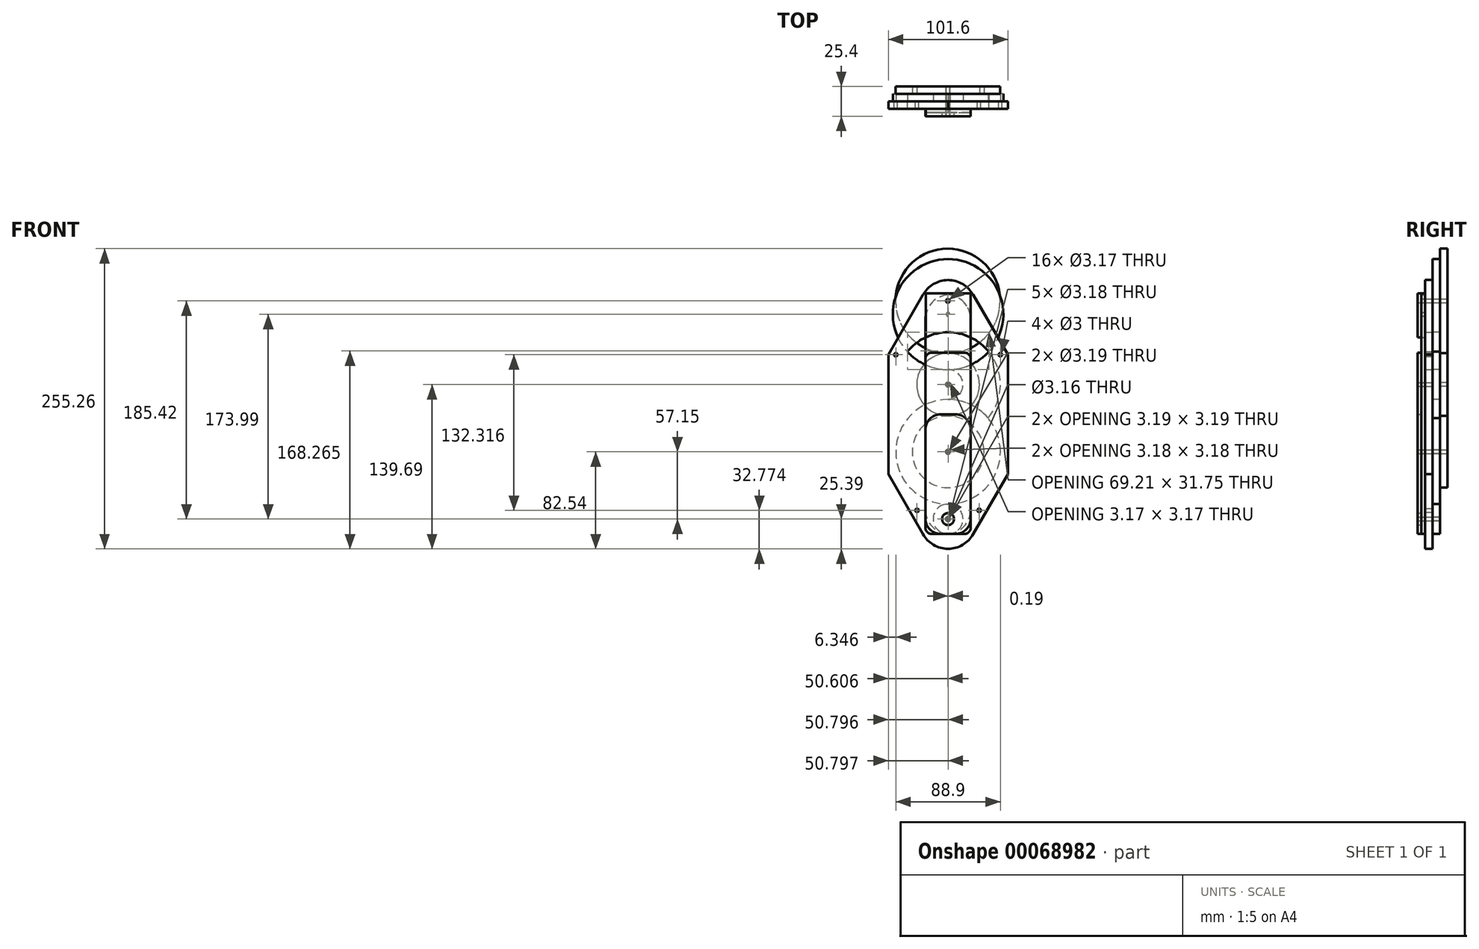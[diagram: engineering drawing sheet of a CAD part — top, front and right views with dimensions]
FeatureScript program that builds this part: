
annotation { "Feature Type Name" : "Feature", "Feature Type Description" : "" }
export const myFeature = defineFeature(function(context is Context, id is Id, definition is map)
    precondition{}
    {
        {
            var Q0;
            Q0=qCreatedBy(makeId("Front.planeOp"),FACE);
            var sketch = newSketch(context, id + "F0", { "sketchPlane" : qUnion([Q0])});
            skLineSegment(sketch, "E0.MirrorCS", {"start": v(51.33, 38.1) * mm, "end": v(22, -12.7) * mm});
            skArc(sketch, "E1.MirrorC", {"start": v(22, -12.7) * mm, "mid": v(12.93, -21.86) * mm, "end": v(0.53, -25.4) * mm});
            skLineSegment(sketch, "E2.MirrorCS", {"start": v(51.33, 38.1) * mm, "end": v(51.33, 88.9) * mm});
            skLineSegment(sketch, "E3", {"start": v(0.53, 88.9) * mm, "end": v(51.33, 88.9) * mm, "construction": true});
            skLineSegment(sketch, "E4", {"start": v(0.53, 88.9) * mm, "end": v(0.53, -25.4) * mm, "construction": true});
            skPoint(sketch, "E5.orphan", {"position": v(-50.27, 88.9) * mm});
            skLineSegment(sketch, "E6.MirrorCS", {"start": v(-50.27, 38.1) * mm, "end": v(-50.27, 88.9) * mm});
            skLineSegment(sketch, "E7.MirrorCS", {"start": v(-50.27, 38.1) * mm, "end": v(-20.94, -12.7) * mm});
            skArc(sketch, "E8.MirrorCS", {"start": v(-20.94, -12.7) * mm, "mid": v(-11.87, -21.86) * mm, "end": v(0.53, -25.4) * mm});
            skLineSegment(sketch, "E9.MirrorCS", {"start": v(-50.27, 139.7) * mm, "end": v(-50.27, 88.9) * mm});
            skLineSegment(sketch, "E10.MirrorCS", {"start": v(51.33, 139.7) * mm, "end": v(22, 190.5) * mm});
            skLineSegment(sketch, "E11.MirrorCS", {"start": v(0.53, 88.9) * mm, "end": v(0.53, 203.2) * mm, "construction": true});
            skArc(sketch, "E12.MirrorCS", {"start": v(22, 190.5) * mm, "mid": v(12.93, 199.66) * mm, "end": v(0.53, 203.2) * mm});
            skArc(sketch, "E13.MirrorCS", {"start": v(-20.94, 190.5) * mm, "mid": v(-11.87, 199.66) * mm, "end": v(0.53, 203.2) * mm});
            skLineSegment(sketch, "E14.MirrorCS", {"start": v(51.33, 139.7) * mm, "end": v(51.33, 88.9) * mm});
            skLineSegment(sketch, "E15.MirrorCS", {"start": v(-50.27, 139.7) * mm, "end": v(-20.94, 190.5) * mm});
            skLineSegment(sketch, "E16", {"start": v(0, 0) * mm, "end": v(1.05, 0) * mm, "construction": true});
            skCircle(sketch, "E17", {"center": v(0.53, 0) * mm, "radius": 12.7 * mm});
            skCircle(sketch, "E18", {"center": v(0.53, 57.15) * mm, "radius": 44.45 * mm});
            skCircle(sketch, "E19", {"center": v(0.53, 57.15) * mm, "radius": 12.7 * mm});
            skCircle(sketch, "E20", {"center": v(0.53, 57.15) * mm, "radius": 1.59 * mm});
            skCircle(sketch, "E21", {"center": v(0.53, 0) * mm, "radius": 1.59 * mm});
            skCircle(sketch, "E22", {"center": v(0.53, 114.3) * mm, "radius": 44.45 * mm});
            skCircle(sketch, "E23", {"center": v(0.53, 114.3) * mm, "radius": 12.7 * mm});
            skCircle(sketch, "E24", {"center": v(0.53, 114.3) * mm, "radius": 1.59 * mm});
            skCircle(sketch, "E25", {"center": v(0.53, 174) * mm, "radius": 47 * mm});
            skSolve(sketch);
        }
        {
            var Q0;
            Q0=makeQuery(id+"F0.imprint","IMPRINT",FACE,{"disambiguationData":[TD([[makeQuery(id+"F0.imprint","IMPRINT",EDGE,{"derivedFrom":sQuery(id+"F0.wireOp",EDGE,"E0.MirrorCS")}),-1.0]])]});
            var Q1;
            {var subQ6=sQuery(id+"F0.wireOp",EDGE,"E12.MirrorCS");Q1=makeQuery(id+"F0.imprint","IMPRINT",FACE,{"disambiguationData":[TD([[makeQuery(id+"F0.imprint","IMPRINT",EDGE,{"derivedFrom":subQ6}),1.0]])]});}
            var Q2;
            {var subQ0=sQuery(id+"F0.wireOp",EDGE,"E23");var subQ1=sQuery(id+"F0.wireOp",EDGE,"E18");var subQ2=makeQuery(id+"F0.imprint","INTERSECT",VERTEX,{"derivedFrom":[subQ1,subQ0]});Q2=makeQuery(id+"F0.imprint","IMPRINT",FACE,{"disambiguationData":[TD([[makeQuery(id+"F0.imprint","IMPRINT",EDGE,{"disambiguationData":[TD([[subQ2,1.0]])],"derivedFrom":subQ1}),-1.0]])]});}
            var Q3;
            {var subQ0=sQuery(id+"F0.wireOp",EDGE,"E25");var subQ1=sQuery(id+"F0.wireOp",EDGE,"E22");var subQ2=makeQuery(id+"F0.imprint","INTERSECT",VERTEX,{"disambiguationData":[OD(0.0)],"derivedFrom":[subQ1,subQ0]});Q3=makeQuery(id+"F0.imprint","IMPRINT",FACE,{"disambiguationData":[TD([[makeQuery(id+"F0.imprint","IMPRINT",EDGE,{"disambiguationData":[TD([[subQ2,1.0]])],"derivedFrom":subQ1}),1.0]])]});}
            var Q4;
            {var subQ0=sQuery(id+"F0.wireOp",EDGE,"E23");var subQ1=sQuery(id+"F0.wireOp",EDGE,"E18");var subQ2=makeQuery(id+"F0.imprint","INTERSECT",VERTEX,{"derivedFrom":[subQ1,subQ0]});Q4=makeQuery(id+"F0.imprint","IMPRINT",FACE,{"disambiguationData":[TD([[makeQuery(id+"F0.imprint","IMPRINT",EDGE,{"disambiguationData":[TD([[subQ2,-1.0]])],"derivedFrom":subQ1}),-1.0]])]});}
            var Q5;
            {var subQ0=sQuery(id+"F0.wireOp",EDGE,"E18");var subQ1=makeQuery(id+"F0.imprint","INTERSECT",VERTEX,{"derivedFrom":[subQ0,sQuery(id+"F0.wireOp",EDGE,"E23")]});Q5=makeQuery(id+"F0.imprint","IMPRINT",FACE,{"disambiguationData":[TD([[makeQuery(id+"F0.imprint","IMPRINT",EDGE,{"disambiguationData":[TD([[subQ1,1.0]])],"derivedFrom":subQ0}),1.0]])]});}
            var Q6;
            Q6=makeQuery(id+"F0.imprint","IMPRINT",FACE,{"disambiguationData":[TD([[makeQuery(id+"F0.imprint","IMPRINT",EDGE,{"derivedFrom":sQuery(id+"F0.wireOp",EDGE,"E24")}),-1.0]])]});
            var Q7;
            Q7=makeQuery(id+"F0.imprint","IMPRINT",FACE,{"disambiguationData":[TD([[makeQuery(id+"F0.imprint","IMPRINT",EDGE,{"derivedFrom":sQuery(id+"F0.wireOp",EDGE,"E19")}),1.0]])]});
            var Q8;
            {var subQ1=sQuery(id+"F0.wireOp",EDGE,"E19");Q8=makeQuery(id+"F0.imprint","IMPRINT",FACE,{"disambiguationData":[TD([[makeQuery(id+"F0.imprint","IMPRINT",EDGE,{"derivedFrom":subQ1}),-1.0]])]});}
            var Q9;
            Q9=makeQuery(id+"F0.imprint","IMPRINT",FACE,{"disambiguationData":[TD([[makeQuery(id+"F0.imprint","IMPRINT",EDGE,{"derivedFrom":sQuery(id+"F0.wireOp",EDGE,"E17")}),1.0]])]});
            extrude(context, id + "F1", {"entities" : qUnion([Q0, Q1, Q2, Q3, Q4, Q5, Q6, Q7, Q8, Q9]), "depth" : 6.35 * mm});
        }
        {
            var Q0;
            {var subQ4=sQuery(id+"F0.wireOp",EDGE,"E12.MirrorCS");Q0=makeQuery(id+"F0.imprint","IMPRINT",FACE,{"disambiguationData":[TD([[makeQuery(id+"F0.imprint","IMPRINT",EDGE,{"derivedFrom":subQ4}),-1.0]])]});}
            var Q1;
            {var subQ6=sQuery(id+"F0.wireOp",EDGE,"E12.MirrorCS");Q1=makeQuery(id+"F0.imprint","IMPRINT",FACE,{"disambiguationData":[TD([[makeQuery(id+"F0.imprint","IMPRINT",EDGE,{"derivedFrom":subQ6}),1.0]])]});}
            var Q2;
            {var subQ0=sQuery(id+"F0.wireOp",EDGE,"E25");var subQ1=sQuery(id+"F0.wireOp",EDGE,"E22");var subQ2=makeQuery(id+"F0.imprint","INTERSECT",VERTEX,{"disambiguationData":[OD(0.0)],"derivedFrom":[subQ1,subQ0]});Q2=makeQuery(id+"F0.imprint","IMPRINT",FACE,{"disambiguationData":[TD([[makeQuery(id+"F0.imprint","IMPRINT",EDGE,{"disambiguationData":[TD([[subQ2,1.0]])],"derivedFrom":subQ1}),1.0]])]});}
            extrude(context, id + "F2", {"entities" : qUnion([Q0, Q1, Q2]), "oppositeDirection" : true, "depth" : 6.35 * mm});
        }
        {
            var Q0;
            {var subQ1=sQuery(id+"F0.wireOp",EDGE,"E19");Q0=makeQuery(id+"F0.imprint","IMPRINT",FACE,{"disambiguationData":[TD([[makeQuery(id+"F0.imprint","IMPRINT",EDGE,{"derivedFrom":subQ1}),-1.0]])]});}
            var Q1;
            {var subQ0=sQuery(id+"F0.wireOp",EDGE,"E18");var subQ1=makeQuery(id+"F0.imprint","INTERSECT",VERTEX,{"derivedFrom":[subQ0,sQuery(id+"F0.wireOp",EDGE,"E23")]});Q1=makeQuery(id+"F0.imprint","IMPRINT",FACE,{"disambiguationData":[TD([[makeQuery(id+"F0.imprint","IMPRINT",EDGE,{"disambiguationData":[TD([[subQ1,1.0]])],"derivedFrom":subQ0}),1.0]])]});}
            var Q2;
            Q2=makeQuery(id+"F0.imprint","IMPRINT",FACE,{"disambiguationData":[TD([[makeQuery(id+"F0.imprint","IMPRINT",EDGE,{"derivedFrom":sQuery(id+"F0.wireOp",EDGE,"E19")}),1.0]])]});
            var Q3;
            Q3=makeQuery(id+"F0.imprint","IMPRINT",FACE,{"disambiguationData":[TD([[makeQuery(id+"F0.imprint","IMPRINT",EDGE,{"derivedFrom":sQuery(id+"F0.wireOp",EDGE,"E17")}),1.0]])]});
            extrude(context, id + "F3", {"entities" : qUnion([Q0, Q1, Q2, Q3]), "oppositeDirection" : true, "depth" : 6.35 * mm});
        }
        {
            var Q0;
            Q0=makeQuery(id+"F0.imprint","IMPRINT",FACE,{"disambiguationData":[TD([[makeQuery(id+"F0.imprint","IMPRINT",EDGE,{"derivedFrom":sQuery(id+"F0.wireOp",EDGE,"E24")}),1.0]])]});
            extrude(context, id + "F4", {"entities" : qUnion([Q0]), "depth" : 101.6 * mm});
        }
        {
            var Q0;
            Q0=makeQuery(id+"F1.opExtrude","CAP_FACE",FACE,{"disambiguationData":[OSD([sQuery(id+"F0.wireOp",EDGE,"E0.MirrorCS"),sQuery(id+"F0.wireOp",EDGE,"E1.MirrorC"),sQuery(id+"F0.wireOp",EDGE,"E2.MirrorCS"),sQuery(id+"F0.wireOp",EDGE,"E6.MirrorCS"),sQuery(id+"F0.wireOp",EDGE,"E7.MirrorCS"),sQuery(id+"F0.wireOp",EDGE,"E8.MirrorCS"),sQuery(id+"F0.wireOp",EDGE,"E9.MirrorCS"),sQuery(id+"F0.wireOp",EDGE,"E10.MirrorCS"),sQuery(id+"F0.wireOp",EDGE,"E12.MirrorCS"),sQuery(id+"F0.wireOp",EDGE,"E13.MirrorCS"),sQuery(id+"F0.wireOp",EDGE,"E14.MirrorCS"),sQuery(id+"F0.wireOp",EDGE,"E15.MirrorCS"),sQuery(id+"F0.wireOp",EDGE,"E20"),sQuery(id+"F0.wireOp",EDGE,"E21"),sQuery(id+"F0.wireOp",EDGE,"E24"),sQuery(id+"F0.wireOp",EDGE,"pjNNc2ZH-NAzS-CAaC-BPgH-MuypsgHAhK5T")])],"isStart":false});
            var sketch = newSketch(context, id + "F5", { "sketchPlane" : qUnion([Q0])});
            skLineSegment(sketch, "E26.bottom", {"start": v(-18.52, 191.77) * mm, "end": v(19.58, 191.77) * mm});
            skLineSegment(sketch, "E26.top", {"start": v(-18.52, 96.52) * mm, "end": v(19.58, 96.52) * mm});
            skLineSegment(sketch, "E26.left", {"start": v(-18.52, 191.77) * mm, "end": v(-18.52, 96.52) * mm});
            skLineSegment(sketch, "E26.right", {"start": v(19.58, 191.77) * mm, "end": v(19.58, 96.52) * mm});
            skSolve(sketch);
        }
        {
            var Q0;
            Q0=makeQuery(id+"F5.imprint","IMPRINT",FACE,{"disambiguationData":[TD([[makeQuery(id+"F5.imprint","IMPRINT",EDGE,{"derivedFrom":sQuery(id+"F5.wireOp",EDGE,"E26.bottom")}),-1.0]])]});
            extrude(context, id + "F6", {"entities" : qUnion([Q0]), "depth" : 6.35 * mm});
        }
        {
            var Q0;
            Q0=makeQuery(id+"F1.opExtrude","CAP_FACE",FACE,{"disambiguationData":[OSD([sQuery(id+"F0.wireOp",EDGE,"E0.MirrorCS"),sQuery(id+"F0.wireOp",EDGE,"E1.MirrorC"),sQuery(id+"F0.wireOp",EDGE,"E2.MirrorCS"),sQuery(id+"F0.wireOp",EDGE,"E6.MirrorCS"),sQuery(id+"F0.wireOp",EDGE,"E7.MirrorCS"),sQuery(id+"F0.wireOp",EDGE,"E8.MirrorCS"),sQuery(id+"F0.wireOp",EDGE,"E9.MirrorCS"),sQuery(id+"F0.wireOp",EDGE,"E10.MirrorCS"),sQuery(id+"F0.wireOp",EDGE,"E12.MirrorCS"),sQuery(id+"F0.wireOp",EDGE,"E13.MirrorCS"),sQuery(id+"F0.wireOp",EDGE,"E14.MirrorCS"),sQuery(id+"F0.wireOp",EDGE,"E15.MirrorCS"),sQuery(id+"F0.wireOp",EDGE,"E20"),sQuery(id+"F0.wireOp",EDGE,"E21"),sQuery(id+"F0.wireOp",EDGE,"E24"),sQuery(id+"F0.wireOp",EDGE,"pjNNc2ZH-NAzS-CAaC-BPgH-MuypsgHAhK5T")])],"isStart":false});
            var sketch = newSketch(context, id + "F7", { "sketchPlane" : qUnion([Q0])});
            skCircle(sketch, "E27", {"center": v(0.53, 0) * mm, "radius": 1.58 * mm});
            skCircle(sketch, "E28", {"center": v(0.53, 57.15) * mm, "radius": 1.59 * mm});
            skCircle(sketch, "E29", {"center": v(0.53, 114.3) * mm, "radius": 1.6 * mm});
            skCircle(sketch, "E30", {"center": v(0.53, 174) * mm, "radius": 1.59 * mm});
            skLineSegment(sketch, "E31.bottom", {"start": v(-18.66, 190.5) * mm, "end": v(19.71, 190.5) * mm});
            skLineSegment(sketch, "E31.top", {"start": v(-18.66, -12.7) * mm, "end": v(19.71, -12.7) * mm});
            skLineSegment(sketch, "E31.left", {"start": v(-18.66, 190.5) * mm, "end": v(-18.66, -12.7) * mm});
            skLineSegment(sketch, "E31.right", {"start": v(19.71, 190.5) * mm, "end": v(19.71, -12.7) * mm});
            skLineSegment(sketch, "E32", {"start": v(-18.66, -12.7) * mm, "end": v(-20.94, -12.7) * mm});
            skLineSegment(sketch, "E33", {"start": v(19.71, -12.7) * mm, "end": v(22, -12.7) * mm});
            skLineSegment(sketch, "E34", {"start": v(0.53, 203.2) * mm, "end": v(0.53, 190.5) * mm});
            skLineSegment(sketch, "E35", {"start": v(0.53, -25.4) * mm, "end": v(0.53, -12.7) * mm});
            skSolve(sketch);
        }
        {
            var Q0;
            Q0 = qSketchRegion(id + "F7", true);
            extrude(context, id + "F8", {"entities" : qUnion([Q0]), "depth" : 3.17 * mm});
        }
        {
            var Q0;
            Q0=makeQuery(id+"F8.opExtrude","SWEPT_EDGE",EDGE,{"disambiguationData":[OSD([sQuery(id+"F7.wireOp",EDGE,"E31.top"),sQuery(id+"F7.wireOp",EDGE,"E31.left"),sQuery(id+"F7.wireOp",EDGE,"E32")])]});
            var Q1;
            Q1=makeQuery(id+"F8.opExtrude","SWEPT_EDGE",EDGE,{"disambiguationData":[OSD([sQuery(id+"F7.wireOp",EDGE,"E31.top"),sQuery(id+"F7.wireOp",EDGE,"E31.right"),sQuery(id+"F7.wireOp",EDGE,"E33")])]});
            var Q2;
            Q2=makeQuery(id+"F8.opExtrude","SWEPT_EDGE",EDGE,{"disambiguationData":[OSD([sQuery(id+"F7.wireOp",EDGE,"E31.bottom"),sQuery(id+"F7.wireOp",EDGE,"E31.right")])]});
            var Q3;
            Q3=makeQuery(id+"F8.opExtrude","SWEPT_EDGE",EDGE,{"disambiguationData":[OSD([sQuery(id+"F7.wireOp",EDGE,"E31.bottom"),sQuery(id+"F7.wireOp",EDGE,"E31.left")])]});
            fillet(context, id + "F9", {"entities" : qUnion([Q0, Q1, Q2, Q3]), "radius" : 20.32 * mm, "tangentPropagation" : true, "allowEdgeOverflow" : false});
        }
        {
            var Q0;
            Q0=makeQuery(id+"F8.opExtrude","CAP_FACE",FACE,{"disambiguationData":[OSD([sQuery(id+"F7.wireOp",EDGE,"E27"),sQuery(id+"F7.wireOp",EDGE,"E28"),sQuery(id+"F7.wireOp",EDGE,"E29"),sQuery(id+"F7.wireOp",EDGE,"E30"),sQuery(id+"F7.wireOp",EDGE,"E31.bottom"),sQuery(id+"F7.wireOp",EDGE,"E31.top"),sQuery(id+"F7.wireOp",EDGE,"E31.left"),sQuery(id+"F7.wireOp",EDGE,"E31.right")])],"isStart":false});
            var sketch = newSketch(context, id + "F10", { "sketchPlane" : qUnion([Q0])});
            skCircle(sketch, "E36", {"center": v(0.53, 0) * mm, "radius": 1.59 * mm});
            skCircle(sketch, "E37", {"center": v(0.53, 0) * mm, "radius": 5.08 * mm});
            skSolve(sketch);
        }
        {
            var Q0;
            Q0 = qSketchRegion(id + "F10", true);
            extrude(context, id + "F11", {"entities" : qUnion([Q0]), "operationType" : NewBodyOperationType.ADD, "depth" : 3.17 * mm});
        }
        {
            var Q0;
            Q0=makeQuery(id+"F8.opExtrude","CAP_FACE",FACE,{"disambiguationData":[OSD([sQuery(id+"F7.wireOp",EDGE,"E27"),sQuery(id+"F7.wireOp",EDGE,"E28"),sQuery(id+"F7.wireOp",EDGE,"E29"),sQuery(id+"F7.wireOp",EDGE,"E30"),sQuery(id+"F7.wireOp",EDGE,"E31.bottom"),sQuery(id+"F7.wireOp",EDGE,"E31.top"),sQuery(id+"F7.wireOp",EDGE,"E31.left"),sQuery(id+"F7.wireOp",EDGE,"E31.right")])],"isStart":false});
            var sketch = newSketch(context, id + "F12", { "sketchPlane" : qUnion([Q0])});
            skCircle(sketch, "E38", {"center": v(0.53, 57.15) * mm, "radius": 1.59 * mm});
            skCircle(sketch, "E39", {"center": v(0.53, 0) * mm, "radius": 1.59 * mm});
            skLineSegment(sketch, "E40.bottom", {"start": v(-18.66, 88.9) * mm, "end": v(19.71, 88.9) * mm});
            skLineSegment(sketch, "E40.top", {"start": v(-18.66, -12.63) * mm, "end": v(19.71, -12.63) * mm});
            skLineSegment(sketch, "E40.left", {"start": v(-18.66, 88.9) * mm, "end": v(-18.66, -12.63) * mm});
            skLineSegment(sketch, "E40.right", {"start": v(19.71, 88.9) * mm, "end": v(19.71, -12.63) * mm});
            skSolve(sketch);
        }
        {
            var Q0;
            Q0 = qSketchRegion(id + "F12", true);
            extrude(context, id + "F13", {"entities" : qUnion([Q0]), "depth" : 3.17 * mm});
        }
        {
            var Q0;
            Q0=makeQuery(id+"F13.opExtrude","SWEPT_EDGE",EDGE,{"disambiguationData":[OSD([sQuery(id+"F12.wireOp",EDGE,"E40.top"),sQuery(id+"F12.wireOp",EDGE,"E40.right")])]});
            var Q1;
            Q1=makeQuery(id+"F13.opExtrude","SWEPT_EDGE",EDGE,{"disambiguationData":[OSD([sQuery(id+"F12.wireOp",EDGE,"E40.top"),sQuery(id+"F12.wireOp",EDGE,"E40.left")])]});
            var Q2;
            Q2=makeQuery(id+"F13.opExtrude","SWEPT_EDGE",EDGE,{"disambiguationData":[OSD([sQuery(id+"F7.wireOp",EDGE,"E31.right"),sQuery(id+"F12.wireOp",EDGE,"E40.bottom"),sQuery(id+"F12.wireOp",EDGE,"E40.right")])]});
            var Q3;
            Q3=makeQuery(id+"F13.opExtrude","SWEPT_EDGE",EDGE,{"disambiguationData":[OSD([sQuery(id+"F7.wireOp",EDGE,"E31.left"),sQuery(id+"F12.wireOp",EDGE,"E40.bottom"),sQuery(id+"F12.wireOp",EDGE,"E40.left")])]});
            fillet(context, id + "F14", {"entities" : qUnion([Q0, Q1, Q2, Q3]), "radius" : 12.7 * mm, "tangentPropagation" : true, "allowEdgeOverflow" : false});
        }
        {
            var Q0;
            Q0=makeQuery(id+"F8.opExtrude","CAP_FACE",FACE,{"disambiguationData":[OSD([sQuery(id+"F7.wireOp",EDGE,"E27"),sQuery(id+"F7.wireOp",EDGE,"E28"),sQuery(id+"F7.wireOp",EDGE,"E29"),sQuery(id+"F7.wireOp",EDGE,"E30"),sQuery(id+"F7.wireOp",EDGE,"E31.bottom"),sQuery(id+"F7.wireOp",EDGE,"E31.top"),sQuery(id+"F7.wireOp",EDGE,"E31.left"),sQuery(id+"F7.wireOp",EDGE,"E31.right")])],"isStart":false});
            var sketch = newSketch(context, id + "F15", { "sketchPlane" : qUnion([Q0])});
            skLineSegment(sketch, "E41.bottom", {"start": v(-18.66, -12.67) * mm, "end": v(19.71, -12.67) * mm});
            skLineSegment(sketch, "E41.top", {"start": v(-18.66, 141.39) * mm, "end": v(19.71, 141.39) * mm});
            skLineSegment(sketch, "E41.left", {"start": v(-18.66, -12.67) * mm, "end": v(-18.66, 141.39) * mm});
            skLineSegment(sketch, "E41.right", {"start": v(19.71, -12.67) * mm, "end": v(19.71, 141.39) * mm});
            skCircle(sketch, "E42", {"center": v(0.53, 114.3) * mm, "radius": 1.59 * mm});
            skCircle(sketch, "E43", {"center": v(0.53, 57.15) * mm, "radius": 1.6 * mm});
            skCircle(sketch, "E44", {"center": v(0.53, 0) * mm, "radius": 1.6 * mm});
            skSolve(sketch);
        }
        {
            var Q0;
            Q0 = qSketchRegion(id + "F15", true);
            extrude(context, id + "F16", {"entities" : qUnion([Q0]), "depth" : 3.17 * mm});
        }
        {
            var Q0;
            Q0=makeQuery(id+"F16.opExtrude","SWEPT_EDGE",EDGE,{"disambiguationData":[OSD([sQuery(id+"F7.wireOp",EDGE,"E31.left"),sQuery(id+"F15.wireOp",EDGE,"E41.top"),sQuery(id+"F15.wireOp",EDGE,"E41.left")])]});
            var Q1;
            Q1=makeQuery(id+"F16.opExtrude","SWEPT_EDGE",EDGE,{"disambiguationData":[OSD([sQuery(id+"F7.wireOp",EDGE,"E31.right"),sQuery(id+"F15.wireOp",EDGE,"E41.top"),sQuery(id+"F15.wireOp",EDGE,"E41.right")])]});
            var Q2;
            Q2=makeQuery(id+"F16.opExtrude","SWEPT_EDGE",EDGE,{"disambiguationData":[OSD([sQuery(id+"F15.wireOp",EDGE,"E41.bottom"),sQuery(id+"F15.wireOp",EDGE,"E41.right")])]});
            var Q3;
            Q3=makeQuery(id+"F16.opExtrude","SWEPT_EDGE",EDGE,{"disambiguationData":[OSD([sQuery(id+"F15.wireOp",EDGE,"E41.bottom"),sQuery(id+"F15.wireOp",EDGE,"E41.left")])]});
            fillet(context, id + "F17", {"entities" : qUnion([Q0, Q1, Q2, Q3]), "radius" : 5.08 * mm, "tangentPropagation" : true, "allowEdgeOverflow" : false});
        }
        {
            var Q0;
            Q0=makeQuery(id+"F1.opExtrude","CAP_FACE",FACE,{"disambiguationData":[OSD([sQuery(id+"F0.wireOp",EDGE,"E0.MirrorCS"),sQuery(id+"F0.wireOp",EDGE,"E1.MirrorC"),sQuery(id+"F0.wireOp",EDGE,"E2.MirrorCS"),sQuery(id+"F0.wireOp",EDGE,"E6.MirrorCS"),sQuery(id+"F0.wireOp",EDGE,"E7.MirrorCS"),sQuery(id+"F0.wireOp",EDGE,"E8.MirrorCS"),sQuery(id+"F0.wireOp",EDGE,"E9.MirrorCS"),sQuery(id+"F0.wireOp",EDGE,"E10.MirrorCS"),sQuery(id+"F0.wireOp",EDGE,"E12.MirrorCS"),sQuery(id+"F0.wireOp",EDGE,"E13.MirrorCS"),sQuery(id+"F0.wireOp",EDGE,"E14.MirrorCS"),sQuery(id+"F0.wireOp",EDGE,"E15.MirrorCS"),sQuery(id+"F0.wireOp",EDGE,"E20"),sQuery(id+"F0.wireOp",EDGE,"E21"),sQuery(id+"F0.wireOp",EDGE,"E24"),sQuery(id+"F0.wireOp",EDGE,"pjNNc2ZH-NAzS-CAaC-BPgH-MuypsgHAhK5T")])],"isStart":true});
            var sketch = newSketch(context, id + "F18", { "sketchPlane" : qUnion([Q0])});
            skCircle(sketch, "E45", {"center": v(-0.53, 0) * mm, "radius": 12.7 * mm});
            skCircle(sketch, "E46", {"center": v(-0.53, 57.15) * mm, "radius": 44.45 * mm});
            skSolve(sketch);
        }
        {
            var Q0;
            Q0 = qSketchRegion(id + "F18", true);
            extrude(context, id + "F19", {"entities" : qUnion([Q0]), "depth" : 6.35 * mm});
        }
        {
            var Q0;
            Q0=makeQuery(id+"F19.opExtrude","CAP_FACE",FACE,{"disambiguationData":[OSD([sQuery(id+"F18.wireOp",EDGE,"E46")])],"isStart":false});
            var sketch = newSketch(context, id + "F20", { "sketchPlane" : qUnion([Q0])});
            skCircle(sketch, "E47", {"center": v(-0.53, 57.15) * mm, "radius": 30.48 * mm});
            skCircle(sketch, "E48.0", {"center": v(-0.53, 114.3) * mm, "radius": 1.59 * mm});
            skCircle(sketch, "E49", {"center": v(-0.53, 114.3) * mm, "radius": 26.67 * mm});
            skCircle(sketch, "E50.0", {"center": v(-0.53, 174) * mm, "radius": 1.59 * mm});
            skCircle(sketch, "E51", {"center": v(-0.34, 185.42) * mm, "radius": 44.45 * mm});
            skSolve(sketch);
        }
        {
            var Q0;
            Q0 = qSketchRegion(id + "F20", true);
            var Q1;
            Q1=makeQuery(id+"F20.imprint","IMPRINT",FACE,{"disambiguationData":[TD([[makeQuery(id+"F20.imprint","IMPRINT",EDGE,{"derivedFrom":sQuery(id+"F20.wireOp",EDGE,"E50.0")}),1.0]])]});
            extrude(context, id + "F21", {"entities" : qUnion([Q0, Q1]), "depth" : 6.35 * mm});
        }
        {
            var Q0;
            Q0=makeQuery(id+"F21.opExtrude","CAP_FACE",FACE,{"disambiguationData":[OSD([sQuery(id+"F20.wireOp",EDGE,"E51")])],"isStart":false});
            var sketch = newSketch(context, id + "F22", { "sketchPlane" : qUnion([Q0])});
            skCircle(sketch, "E52.0", {"center": v(-0.34, 185.42) * mm, "radius": 44.45 * mm, "construction": true});
            skCircle(sketch, "E53.0", {"center": v(-0.53, 114.3) * mm, "radius": 26.67 * mm, "construction": true});
            skCircle(sketch, "E54.0", {"center": v(-0.53, 57.15) * mm, "radius": 30.48 * mm, "construction": true});
            skCircle(sketch, "E55.0", {"center": v(-0.53, 0) * mm, "radius": 12.7 * mm, "construction": true});
            skCircle(sketch, "E56", {"center": v(-0.34, 185.42) * mm, "radius": 1.59 * mm});
            skCircle(sketch, "E57", {"center": v(-0.53, 114.3) * mm, "radius": 1.59 * mm});
            skCircle(sketch, "E58", {"center": v(-0.53, 57.15) * mm, "radius": 1.59 * mm});
            skCircle(sketch, "E59", {"center": v(-0.53, 0) * mm, "radius": 1.59 * mm});
            skSolve(sketch);
        }
        {
            var Q0;
            Q0 = qSketchRegion(id + "F22", true);
            extrude(context, id + "F23", {"entities" : qUnion([Q0]), "operationType" : NewBodyOperationType.REMOVE, "endBound" : BoundingType.THROUGH_ALL, "oppositeDirection" : true, "depth" : 6.35 * mm});
        }
        {
            var Q0;
            Q0=makeQuery(id+"F1.opExtrude","CAP_FACE",FACE,{"disambiguationData":[OSD([sQuery(id+"F0.wireOp",EDGE,"E0.MirrorCS"),sQuery(id+"F0.wireOp",EDGE,"E1.MirrorC"),sQuery(id+"F0.wireOp",EDGE,"E2.MirrorCS"),sQuery(id+"F0.wireOp",EDGE,"E6.MirrorCS"),sQuery(id+"F0.wireOp",EDGE,"E7.MirrorCS"),sQuery(id+"F0.wireOp",EDGE,"E8.MirrorCS"),sQuery(id+"F0.wireOp",EDGE,"E9.MirrorCS"),sQuery(id+"F0.wireOp",EDGE,"E10.MirrorCS"),sQuery(id+"F0.wireOp",EDGE,"E12.MirrorCS"),sQuery(id+"F0.wireOp",EDGE,"E13.MirrorCS"),sQuery(id+"F0.wireOp",EDGE,"E14.MirrorCS"),sQuery(id+"F0.wireOp",EDGE,"E15.MirrorCS"),sQuery(id+"F0.wireOp",EDGE,"E20"),sQuery(id+"F0.wireOp",EDGE,"E21"),sQuery(id+"F0.wireOp",EDGE,"E24")])],"isStart":true});
            var sketch = newSketch(context, id + "F24", { "sketchPlane" : qUnion([Q0])});
            skCircle(sketch, "E60", {"center": v(-44.98, 139.7) * mm, "radius": 1.5 * mm});
            skLineSegment(sketch, "E61", {"start": v(-51.33, 139.7) * mm, "end": v(-44.98, 139.7) * mm, "construction": true});
            skLineSegment(sketch, "E62", {"start": v(-0.53, 203.2) * mm, "end": v(-0.53, -90.86) * mm, "construction": true});
            skCircle(sketch, "E63.MirrorC", {"center": v(-26.92, 7.38) * mm, "radius": 1.5 * mm});
            skCircle(sketch, "E64.MirrorC", {"center": v(43.92, 139.7) * mm, "radius": 1.5 * mm});
            skCircle(sketch, "E65.MirrorC", {"center": v(25.86, 7.38) * mm, "radius": 1.5 * mm});
            skSolve(sketch);
        }
        {
            var Q0;
            Q0 = qSketchRegion(id + "F24", true);
            extrude(context, id + "F25", {"entities" : qUnion([Q0]), "operationType" : NewBodyOperationType.REMOVE, "endBound" : BoundingType.THROUGH_ALL, "oppositeDirection" : true, "depth" : 25.4 * mm});
        }
    });
